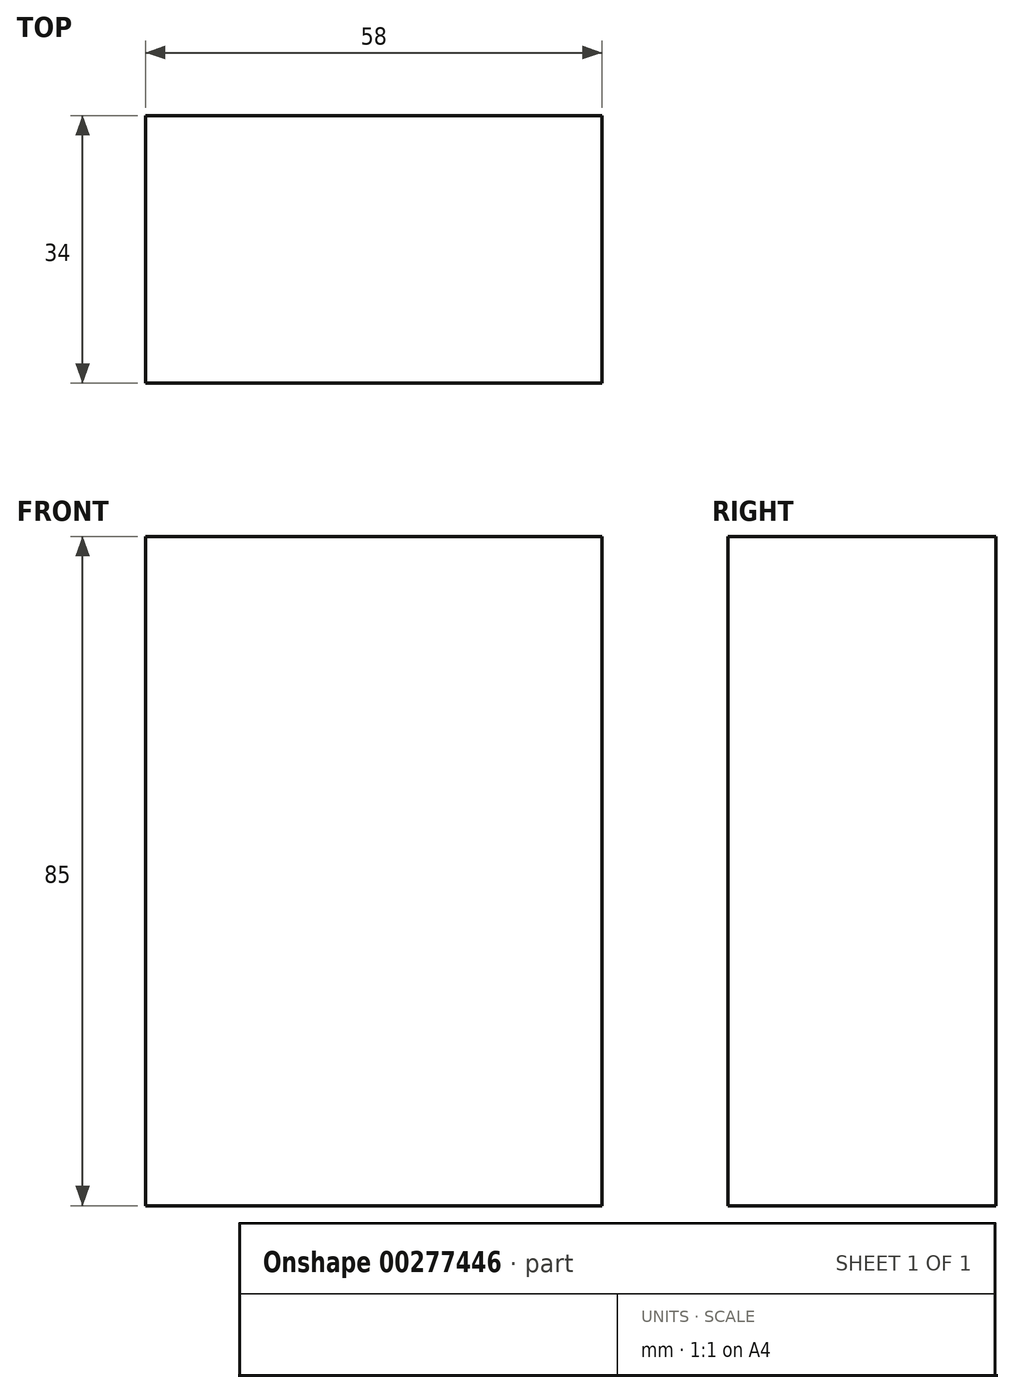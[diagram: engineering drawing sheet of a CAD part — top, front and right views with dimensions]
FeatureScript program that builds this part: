
annotation { "Feature Type Name" : "Feature", "Feature Type Description" : "" }
export const myFeature = defineFeature(function(context is Context, id is Id, definition is map)
    precondition{}
    {
        {
            var Q0;
            Q0=qCreatedBy(makeId("Front.planeOp"),FACE);
            var sketch = newSketch(context, id + "F0", { "sketchPlane" : qUnion([Q0])});
            skLineSegment(sketch, "E0.bottom", {"start": v(29, 42.5) * mm, "end": v(-29, 42.5) * mm});
            skLineSegment(sketch, "E0.top", {"start": v(29, -42.5) * mm, "end": v(-29, -42.5) * mm});
            skLineSegment(sketch, "E0.left", {"start": v(29, 42.5) * mm, "end": v(29, -42.5) * mm});
            skLineSegment(sketch, "E0.right", {"start": v(-29, 42.5) * mm, "end": v(-29, -42.5) * mm});
            skPoint(sketch, "E0.middle", {"position": v(0, 0) * mm});
            skSolve(sketch);
        }
        {
            var Q0;
            Q0=makeQuery(id+"F0.imprint","IMPRINT",FACE,{"disambiguationData":[TD([[makeQuery(id+"F0.imprint","IMPRINT",EDGE,{"derivedFrom":sQuery(id+"F0.wireOp",EDGE,"E0.bottom")}),1.0]])]});
            extrude(context, id + "F1", {"entities" : qUnion([Q0]), "depth" : 34 * mm});
        }
    });
